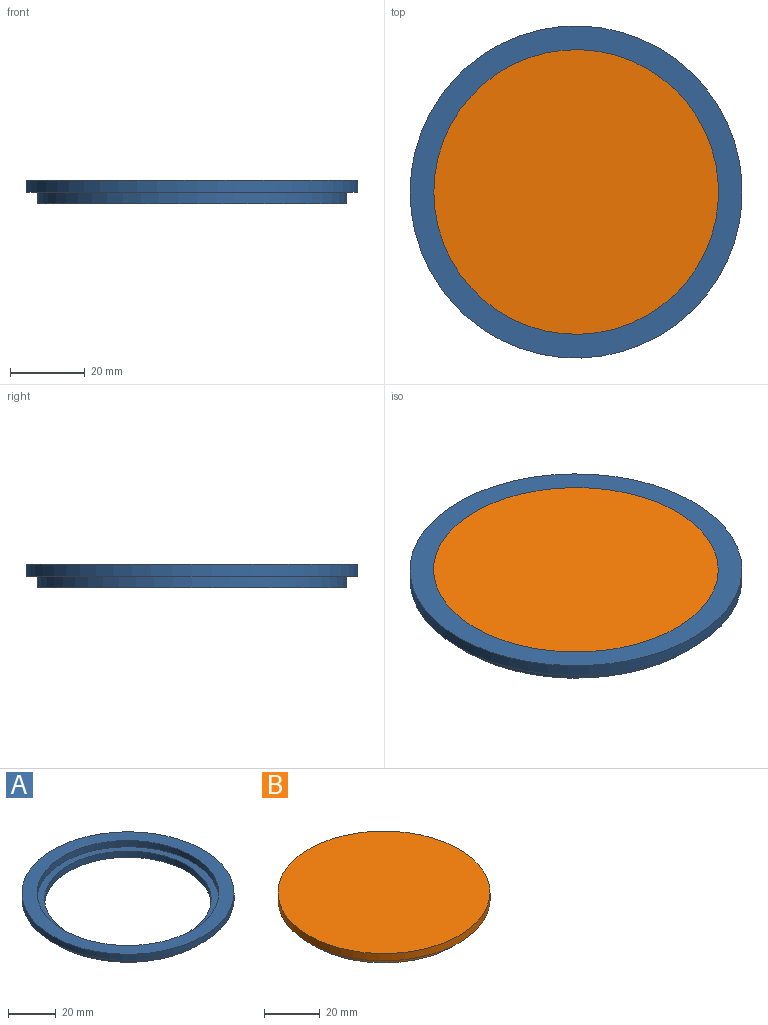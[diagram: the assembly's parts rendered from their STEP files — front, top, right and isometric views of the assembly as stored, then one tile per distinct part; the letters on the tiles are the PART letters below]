
ASSEMBLY  parts=2 mates=1
PART A: 8 faces, bbox 88.9x88.9x6.4 mm
  f0: cylinder r=34.92mm len=69.85mm, axis (0,0,-1), area 696.7mm2, adj f1,f7
  f1: plane 76.2x76.2mm, normal (0,0,1), area 728.4mm2, adj f0,f2
  f2: cylinder r=38.1mm len=76.2mm, axis (0,0,-1), area 760.1mm2, adj f1,f3
  f3: plane 88.9x88.9mm, normal (0,0,1), area 1646.8mm2, adj f2,f4
  f4: cylinder r=44.45mm len=88.9mm, axis (0,0,-1), area 886.7mm2, adj f3,f5
  f5: plane 88.9x88.9mm, normal (0,0,-1), area 855.1mm2, adj f4,f6
  f6: cylinder r=41.27mm len=82.55mm, axis (0,0,-1), area 823.4mm2, adj f5,f7
  f7: plane 82.55x82.55mm, normal (0,0,-1), area 1520.1mm2, adj f0,f6
PART B: 5 faces, bbox 76.2x76.2x6.4 mm
  f0: plane 76.2x76.2mm, normal (0,0,1), area 4560.4mm2, adj f1
  f1: cylinder r=38.1mm len=76.2mm, axis (0,0,-1), area 760.1mm2, adj f0,f2
  f2: plane 76.2x76.2mm, normal (0,0,-1), area 728.4mm2, adj f1,f3
  f3: cylinder r=34.92mm len=69.85mm, axis (0,0,-1), area 696.7mm2, adj f2,f4
  f4: plane 69.85x69.85mm, normal (0,0,-1), area 3832mm2, adj f3
PLACE A t=(-12.06,-6.78,-2.9)mm fixed
PLACE B t=(-12.06,-6.78,-2.9)mm
MATE slider B.f1 <-> A.f0  axis (0,0,1) through (-12.06,-6.78,3.45)mm
